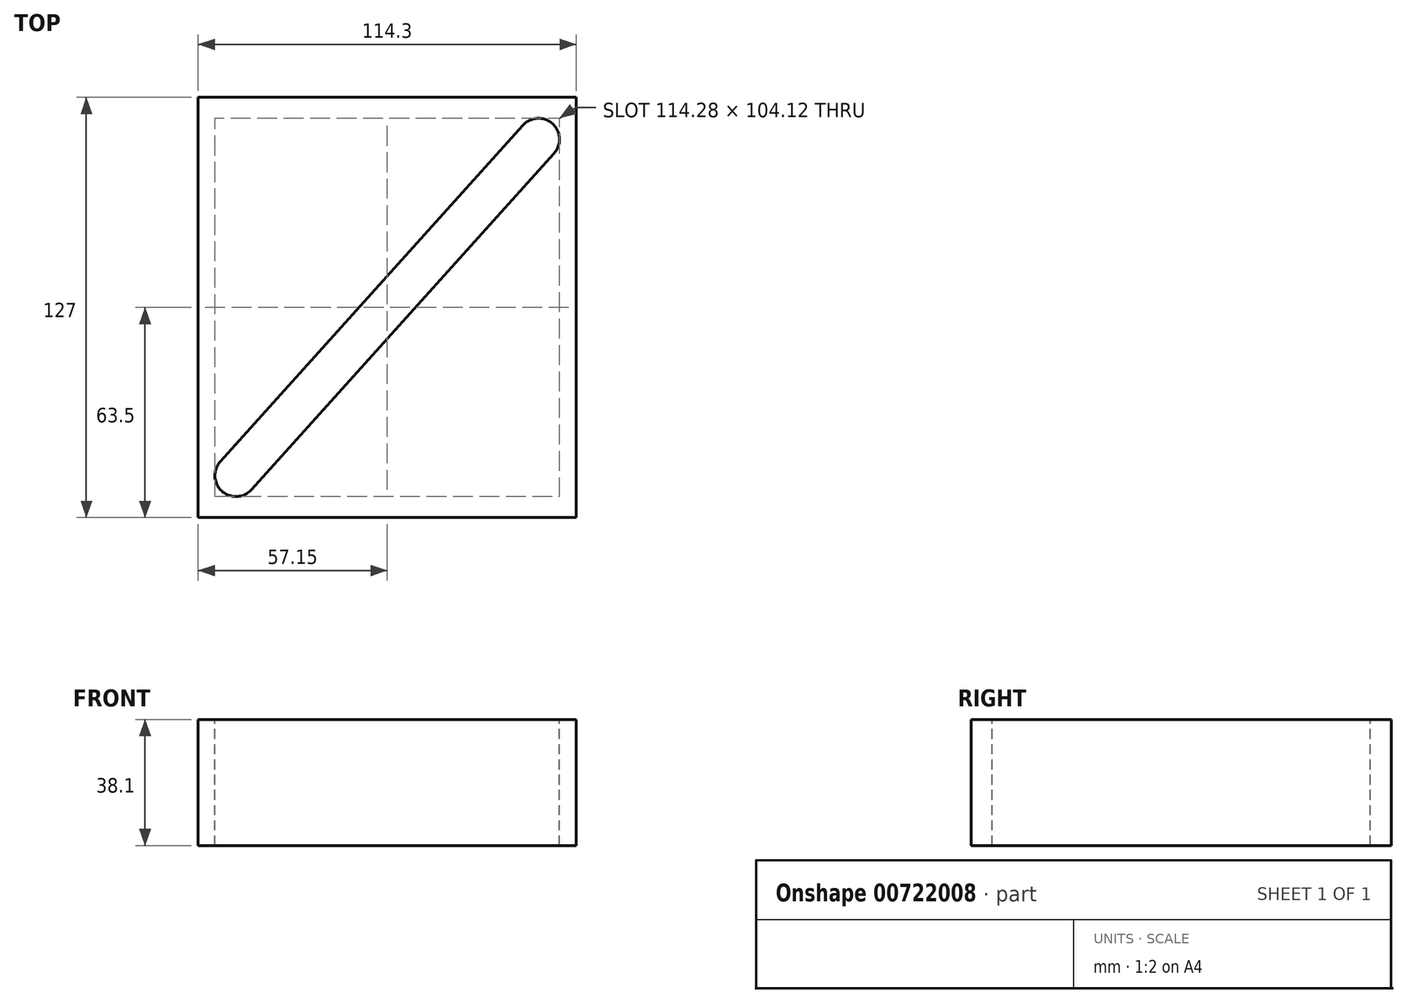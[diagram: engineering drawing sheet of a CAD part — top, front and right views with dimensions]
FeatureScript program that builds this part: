
annotation { "Feature Type Name" : "Feature", "Feature Type Description" : "" }
export const myFeature = defineFeature(function(context is Context, id is Id, definition is map)
    precondition{}
    {
        {
            var Q0;
            Q0=qCreatedBy(makeId("Front.planeOp"),FACE);
            var sketch = newSketch(context, id + "F0", { "sketchPlane" : qUnion([Q0])});
            skLineSegment(sketch, "E0.bottom", {"start": v(57.15, -19.05) * mm, "end": v(-57.15, -19.05) * mm});
            skLineSegment(sketch, "E0.top", {"start": v(57.15, 19.05) * mm, "end": v(-57.15, 19.05) * mm});
            skLineSegment(sketch, "E0.left", {"start": v(57.15, -19.05) * mm, "end": v(57.15, 19.05) * mm});
            skLineSegment(sketch, "E0.right", {"start": v(-57.15, -19.05) * mm, "end": v(-57.15, 19.05) * mm});
            skPoint(sketch, "E0.middle", {"position": v(0, 0) * mm});
            skSolve(sketch);
        }
        {
            var Q0;
            Q0=makeQuery(id+"F0.imprint","IMPRINT",FACE,{"disambiguationData":[TD([[makeQuery(id+"F0.imprint","IMPRINT",EDGE,{"derivedFrom":sQuery(id+"F0.wireOp",EDGE,"E0.bottom")}),-1.0]])]});
            extrude(context, id + "F1", {"entities" : qUnion([Q0]), "depth" : 127 * mm, "offsetDistance" : 25.4 * mm});
        }
        {
            var Q0;
            Q0=makeQuery(id+"F1.opExtrude","SWEPT_FACE",FACE,{"disambiguationData":[OSD([sQuery(id+"F0.wireOp",EDGE,"E0.top")])]});
            var sketch = newSketch(context, id + "F2", { "sketchPlane" : qUnion([Q0])});
            skLineSegment(sketch, "E1.0", {"start": v(-57.15, -127) * mm, "end": v(-57.15, 0) * mm});
            skLineSegment(sketch, "E2.0", {"start": v(57.15, -127) * mm, "end": v(57.15, 0) * mm});
            skLineSegment(sketch, "E3.0", {"start": v(57.15, -127) * mm, "end": v(-57.15, -127) * mm});
            skLineSegment(sketch, "E4.0", {"start": v(57.15, 0) * mm, "end": v(-57.15, 0) * mm});
            skLineSegment(sketch, "E5", {"start": v(-57.15, -127) * mm, "end": v(57.15, 0) * mm, "construction": true});
            skCircle(sketch, "E6", {"center": v(-45.72, -114.3) * mm, "radius": 6.35 * mm});
            skLineSegment(sketch, "E7", {"start": v(57.15, -127) * mm, "end": v(-57.15, 0) * mm, "construction": true});
            skCircle(sketch, "E8", {"center": v(45.72, -12.7) * mm, "radius": 6.35 * mm});
            skLineSegment(sketch, "E9", {"start": v(-50.43, -110.04) * mm, "end": v(40.99, -8.47) * mm});
            skLineSegment(sketch, "E10.MirrorCS", {"start": v(-40.99, -118.53) * mm, "end": v(50.43, -16.96) * mm});
            skSolve(sketch);
        }
        {
            var Q0;
            {var subQ0=sQuery(id+"F2.wireOp",EDGE,"E9");Q0=makeQuery(id+"F2.imprint","IMPRINT",FACE,{"disambiguationData":[TD([[makeQuery(id+"F2.imprint","IMPRINT",EDGE,{"derivedFrom":subQ0}),-1.0]])]});}
            var Q1;
            {var subQ0=sQuery(id+"F2.wireOp",EDGE,"E6");var subQ1=makeQuery(id+"F2.imprint","INTERSECT",VERTEX,{"derivedFrom":[subQ0,sQuery(id+"F2.wireOp",EDGE,"E9")]});Q1=makeQuery(id+"F2.imprint","IMPRINT",FACE,{"disambiguationData":[TD([[makeQuery(id+"F2.imprint","IMPRINT",EDGE,{"disambiguationData":[TD([[subQ1,-1.0]])],"derivedFrom":subQ0}),1.0]])]});}
            var Q2;
            {var subQ0=sQuery(id+"F2.wireOp",EDGE,"E8");var subQ1=makeQuery(id+"F2.imprint","INTERSECT",VERTEX,{"derivedFrom":[subQ0,sQuery(id+"F2.wireOp",EDGE,"E9")]});Q2=makeQuery(id+"F2.imprint","IMPRINT",FACE,{"disambiguationData":[TD([[makeQuery(id+"F2.imprint","IMPRINT",EDGE,{"disambiguationData":[TD([[subQ1,-1.0]])],"derivedFrom":subQ0}),1.0]])]});}
            extrude(context, id + "F3", {"entities" : qUnion([Q0, Q1, Q2]), "operationType" : NewBodyOperationType.REMOVE, "endBound" : BoundingType.THROUGH_ALL, "oppositeDirection" : true, "depth" : 25.4 * mm, "offsetDistance" : 25.4 * mm});
        }
    });
